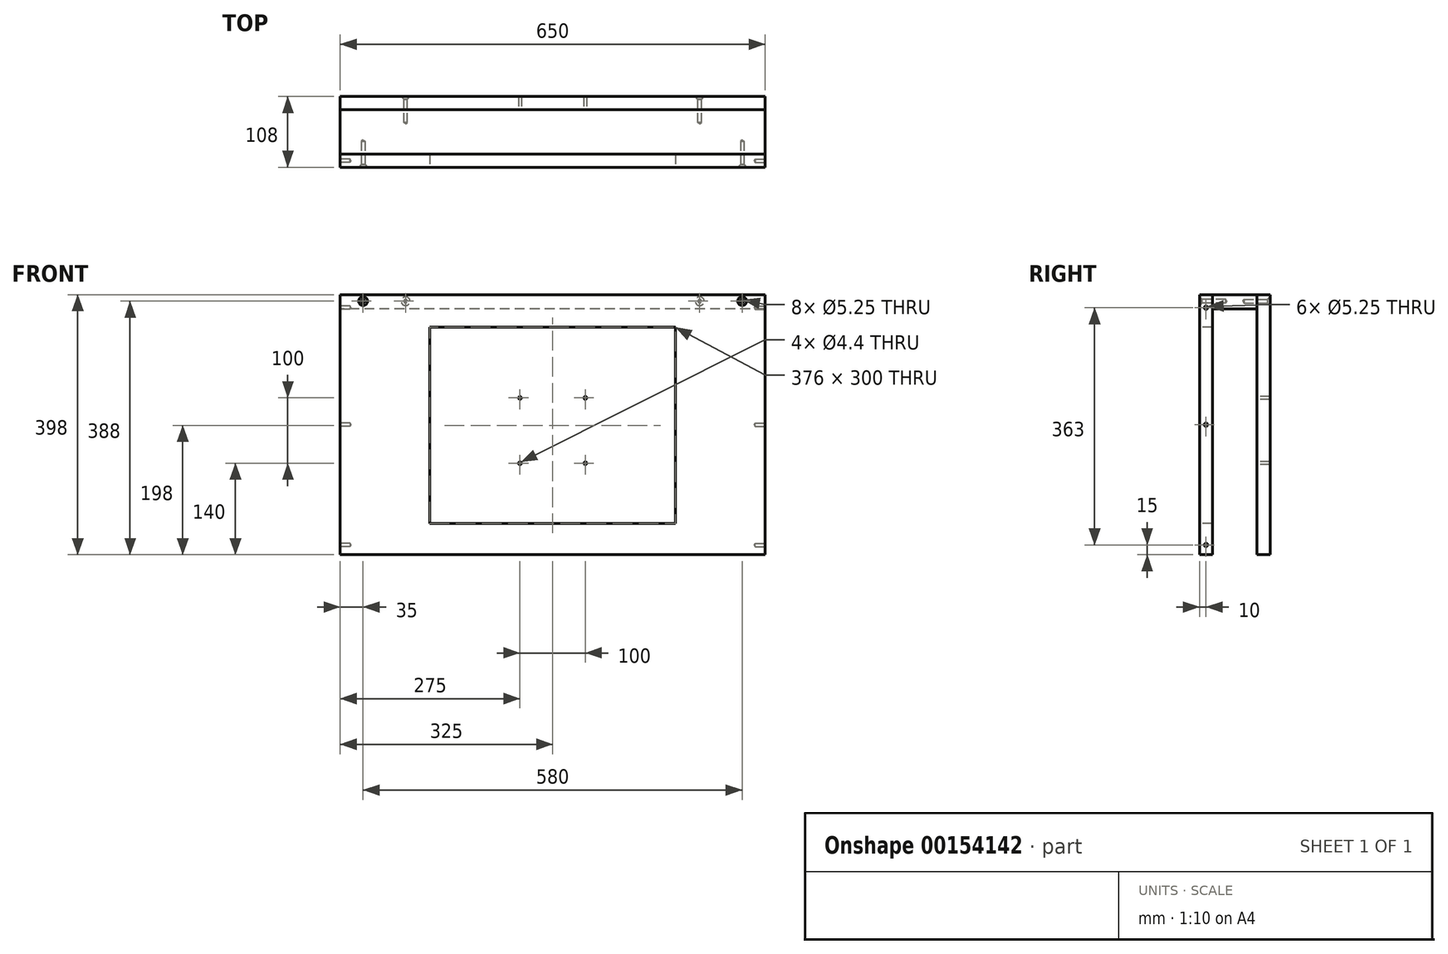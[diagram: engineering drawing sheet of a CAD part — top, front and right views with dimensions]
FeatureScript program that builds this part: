
annotation { "Feature Type Name" : "Feature", "Feature Type Description" : "" }
export const myFeature = defineFeature(function(context is Context, id is Id, definition is map)
    precondition{}
    {
        {
            var Q0;
            Q0=qCreatedBy(makeId("Front.planeOp"),FACE);
            var sketch = newSketch(context, id + "F0", { "sketchPlane" : qUnion([Q0])});
            skLineSegment(sketch, "E0.bottom", {"start": v(325, -199) * mm, "end": v(-325, -199) * mm});
            skLineSegment(sketch, "E0.top", {"start": v(325, 199) * mm, "end": v(-325, 199) * mm});
            skLineSegment(sketch, "E0.left", {"start": v(325, -199) * mm, "end": v(325, 199) * mm});
            skLineSegment(sketch, "E0.right", {"start": v(-325, -199) * mm, "end": v(-325, 199) * mm});
            skPoint(sketch, "E0.middle", {"position": v(0, 0) * mm});
            skLineSegment(sketch, "E1.bottom", {"start": v(-188, 149) * mm, "end": v(188, 149) * mm});
            skLineSegment(sketch, "E1.top", {"start": v(-188, -151) * mm, "end": v(188, -151) * mm});
            skLineSegment(sketch, "E1.left", {"start": v(-188, 149) * mm, "end": v(-188, -151) * mm});
            skLineSegment(sketch, "E1.right", {"start": v(188, 149) * mm, "end": v(188, -151) * mm});
            skPoint(sketch, "E2", {"position": v(-290, 189) * mm});
            skPoint(sketch, "E3", {"position": v(290, 189) * mm});
            skSolve(sketch);
        }
        {
            var Q0;
            Q0 = qSketchRegion(id + "F0", true);
            extrude(context, id + "F1", {"entities" : qUnion([Q0]), "oppositeDirection" : true, "depth" : 20 * mm});
        }
        {
            var Q0;
            Q0=makeQuery(id+"F1.opExtrude","SWEPT_FACE",FACE,{"disambiguationData":[OSD([sQuery(id+"F0.wireOp",EDGE,"E0.right")])]});
            var sketch = newSketch(context, id + "F2", { "sketchPlane" : qUnion([Q0])});
            skLineSegment(sketch, "E4.bottom", {"start": v(-20, 199) * mm, "end": v(0, 199) * mm});
            skLineSegment(sketch, "E4.top", {"start": v(-20, -199) * mm, "end": v(0, -199) * mm});
            skLineSegment(sketch, "E4.left", {"start": v(-20, 199) * mm, "end": v(-20, -199) * mm});
            skLineSegment(sketch, "E4.right", {"start": v(0, 199) * mm, "end": v(0, -199) * mm});
            skPoint(sketch, "E5", {"position": v(-10, 179) * mm});
            skPoint(sketch, "E6", {"position": v(-10, 0) * mm});
            skPoint(sketch, "E7", {"position": v(-10, -184) * mm});
            skSolve(sketch);
        }
        {
            var Q0;
            Q0=makeQuery(id+"F1.opExtrude","SWEPT_FACE",FACE,{"disambiguationData":[OSD([sQuery(id+"F0.wireOp",EDGE,"E0.left")])]});
            var sketch = newSketch(context, id + "F3", { "sketchPlane" : qUnion([Q0])});
            skPoint(sketch, "E8", {"position": v(10, 0) * mm});
            skPoint(sketch, "E9", {"position": v(10, 179) * mm});
            skPoint(sketch, "E10", {"position": v(10, -184) * mm});
            skSolve(sketch);
        }
        {
            var Q0;
            Q0=sQuery(id+"F2.wireOp",VERTEX,"E5");
            var Q1;
            Q1=sQuery(id+"F2.wireOp",VERTEX,"E6");
            var Q2;
            Q2=sQuery(id+"F2.wireOp",VERTEX,"E7");
            var Q3;
            Q3=sQuery(id+"F3.wireOp",VERTEX,"E9");
            var Q4;
            Q4=sQuery(id+"F3.wireOp",VERTEX,"E8");
            var Q5;
            Q5=sQuery(id+"F3.wireOp",VERTEX,"E10");
            var Q6;
            Q6=makeQuery(id+"F1.opExtrude","SWEPT_BODY",BODY,{"disambiguationData":[OSD([sQuery(id+"F0.wireOp",EDGE,"E0.bottom"),sQuery(id+"F0.wireOp",EDGE,"E0.top"),sQuery(id+"F0.wireOp",EDGE,"E0.left"),sQuery(id+"F0.wireOp",EDGE,"E0.right"),sQuery(id+"F0.wireOp",EDGE,"E1.bottom"),sQuery(id+"F0.wireOp",EDGE,"E1.top"),sQuery(id+"F0.wireOp",EDGE,"E1.left"),sQuery(id+"F0.wireOp",EDGE,"E1.right")])]});
            hole(context, id + "F4", {"style" : HoleStyle.SIMPLE, "endStyle" : HoleEndStyle.BLIND, "standardTappedOrClearance" : lookupTablePath({ "standard" : "ISO", "engagement" : "75%", "pitch" : "0.75 mm", "size" : "M6", "type" : "Tapped" }), "standardBlindInLast" : lookupTablePath({ "standard" : "ISO", "engagement" : "75%", "pitch" : "0.75 mm", "size" : "M6", "type" : "Tapped" }), "holeDiameter" : 5.25 * mm, "holeDepth" : 15 * mm, "locations" : qUnion([Q0, Q1, Q2, Q3, Q4, Q5]), "scope" : qUnion([Q6]), "majorDiameter" : 6 * mm});
        }
        {
            var Q0;
            Q0=makeQuery(id+"F1.opExtrude","CAP_FACE",FACE,{"disambiguationData":[OSD([sQuery(id+"F0.wireOp",EDGE,"E0.bottom"),sQuery(id+"F0.wireOp",EDGE,"E0.top"),sQuery(id+"F0.wireOp",EDGE,"E0.left"),sQuery(id+"F0.wireOp",EDGE,"E0.right"),sQuery(id+"F0.wireOp",EDGE,"E1.bottom"),sQuery(id+"F0.wireOp",EDGE,"E1.top"),sQuery(id+"F0.wireOp",EDGE,"E1.left"),sQuery(id+"F0.wireOp",EDGE,"E1.right")])],"isStart":false});
            var sketch = newSketch(context, id + "F5", { "sketchPlane" : qUnion([Q0])});
            skLineSegment(sketch, "E11.bottom", {"start": v(-325, 199) * mm, "end": v(325, 199) * mm});
            skLineSegment(sketch, "E11.top", {"start": v(-325, 177) * mm, "end": v(325, 177) * mm});
            skLineSegment(sketch, "E11.left", {"start": v(325, 199) * mm, "end": v(325, 177) * mm});
            skLineSegment(sketch, "E11.right", {"start": v(-325, 199) * mm, "end": v(-325, 177) * mm});
            skSolve(sketch);
        }
        {
            var Q0;
            Q0 = qSketchRegion(id + "F5", true);
            extrude(context, id + "F6", {"entities" : qUnion([Q0]), "depth" : 68 * mm});
        }
        {
            var Q0;
            Q0=makeQuery(id+"F6.opExtrude","CAP_FACE",FACE,{"disambiguationData":[OSD([sQuery(id+"F5.wireOp",EDGE,"E11.bottom"),sQuery(id+"F5.wireOp",EDGE,"E11.top"),sQuery(id+"F5.wireOp",EDGE,"E11.left"),sQuery(id+"F5.wireOp",EDGE,"E11.right")])],"isStart":false});
            var sketch = newSketch(context, id + "F7", { "sketchPlane" : qUnion([Q0])});
            skLineSegment(sketch, "E12.bottom", {"start": v(-325, 199) * mm, "end": v(325, 199) * mm});
            skLineSegment(sketch, "E12.top", {"start": v(-325, -199) * mm, "end": v(325, -199) * mm});
            skLineSegment(sketch, "E12.left", {"start": v(-325, 199) * mm, "end": v(-325, -199) * mm});
            skLineSegment(sketch, "E12.right", {"start": v(325, 199) * mm, "end": v(325, -199) * mm});
            skPoint(sketch, "E13", {"position": v(-50, 41) * mm});
            skPoint(sketch, "E14", {"position": v(-50, -59) * mm});
            skPoint(sketch, "E15", {"position": v(50, -59) * mm});
            skPoint(sketch, "E16", {"position": v(50, 41) * mm});
            skLineSegment(sketch, "E17", {"start": v(-50, -59) * mm, "end": v(50, -59) * mm});
            skLineSegment(sketch, "E18", {"start": v(-50, 41) * mm, "end": v(50, 41) * mm});
            skLineSegment(sketch, "E19", {"start": v(50, 41) * mm, "end": v(50, -59) * mm});
            skLineSegment(sketch, "E20", {"start": v(-50, -59) * mm, "end": v(-50, 41) * mm});
            skSolve(sketch);
        }
        {
            var Q0;
            Q0 = qSketchRegion(id + "F7", true);
            var Q1;
            Q1=makeQuery(id+"F7.imprint","IMPRINT",FACE,{"disambiguationData":[TD([[makeQuery(id+"F7.imprint","IMPRINT",EDGE,{"derivedFrom":sQuery(id+"F7.wireOp",EDGE,"E17")}),1.0]])]});
            extrude(context, id + "F8", {"entities" : qUnion([Q0, Q1]), "depth" : 20 * mm});
        }
        {
            var Q0;
            Q0=makeQuery(id+"F8.opExtrude","CAP_FACE",FACE,{"disambiguationData":[OSD([sQuery(id+"F7.wireOp",EDGE,"E12.bottom"),sQuery(id+"F7.wireOp",EDGE,"E12.top"),sQuery(id+"F7.wireOp",EDGE,"E12.left"),sQuery(id+"F7.wireOp",EDGE,"E12.right")])],"isStart":false});
            var sketch = newSketch(context, id + "F9", { "sketchPlane" : qUnion([Q0])});
            skLineSegment(sketch, "E21.bottom", {"start": v(-325, 199) * mm, "end": v(325, 199) * mm});
            skLineSegment(sketch, "E21.top", {"start": v(-325, -199) * mm, "end": v(325, -199) * mm});
            skLineSegment(sketch, "E21.left", {"start": v(-325, 199) * mm, "end": v(-325, -199) * mm});
            skLineSegment(sketch, "E21.right", {"start": v(325, 199) * mm, "end": v(325, -199) * mm});
            skPoint(sketch, "E22", {"position": v(-225, 189) * mm});
            skPoint(sketch, "E23", {"position": v(225, 189) * mm});
            skSolve(sketch);
        }
        {
            var Q0;
            Q0=sQuery(id+"F0.wireOp",VERTEX,"E2");
            var Q1;
            Q1=sQuery(id+"F0.wireOp",VERTEX,"E3");
            var Q2;
            Q2=sQuery(id+"F9.wireOp",VERTEX,"E22");
            var Q3;
            Q3=sQuery(id+"F9.wireOp",VERTEX,"E23");
            var Q4;
            Q4=makeQuery(id+"F1.opExtrude","SWEPT_BODY",BODY,{"disambiguationData":[OSD([sQuery(id+"F0.wireOp",EDGE,"E0.bottom"),sQuery(id+"F0.wireOp",EDGE,"E0.top"),sQuery(id+"F0.wireOp",EDGE,"E0.left"),sQuery(id+"F0.wireOp",EDGE,"E0.right"),sQuery(id+"F0.wireOp",EDGE,"E1.bottom"),sQuery(id+"F0.wireOp",EDGE,"E1.top"),sQuery(id+"F0.wireOp",EDGE,"E1.left"),sQuery(id+"F0.wireOp",EDGE,"E1.right")])]});
            var Q5;
            Q5=makeQuery(id+"F6.opExtrude","SWEPT_BODY",BODY,{"disambiguationData":[OSD([sQuery(id+"F5.wireOp",EDGE,"E11.bottom"),sQuery(id+"F5.wireOp",EDGE,"E11.top"),sQuery(id+"F5.wireOp",EDGE,"E11.left"),sQuery(id+"F5.wireOp",EDGE,"E11.right")])]});
            var Q6;
            Q6=makeQuery(id+"F8.opExtrude","SWEPT_BODY",BODY,{"disambiguationData":[OSD([sQuery(id+"F7.wireOp",EDGE,"E12.bottom"),sQuery(id+"F7.wireOp",EDGE,"E12.top"),sQuery(id+"F7.wireOp",EDGE,"E12.left"),sQuery(id+"F7.wireOp",EDGE,"E12.right")])]});
            hole(context, id + "F10", {"style" : HoleStyle.C_SINK, "endStyle" : HoleEndStyle.BLIND, "standardTappedOrClearance" : lookupTablePath({ "standard" : "ISO", "engagement" : "75%", "pitch" : "0.75 mm", "size" : "M6", "type" : "Tapped" }), "standardBlindInLast" : lookupTablePath({ "standard" : "ISO", "engagement" : "75%", "pitch" : "0.75 mm", "size" : "M6", "type" : "Tapped" }), "holeDiameter" : 5.25 * mm, "cSinkDiameter" : 13.44 * mm, "cSinkAngle" : 90 * degree, "holeDepth" : 40 * mm, "locations" : qUnion([Q0, Q1, Q2, Q3]), "scope" : qUnion([Q4, Q5, Q6]), "majorDiameter" : 6 * mm});
        }
        {
            var Q0;
            Q0=sQuery(id+"F7.wireOp",VERTEX,"E13");
            var Q1;
            Q1=sQuery(id+"F7.wireOp",VERTEX,"0c5c716c-c621-4fc1-a947-26692eb2ba86");
            var Q2;
            Q2=sQuery(id+"F7.wireOp",VERTEX,"0617914d-727d-4c80-badd-26484117caa5");
            var Q3;
            Q3=sQuery(id+"F7.wireOp",VERTEX,"96a15a45-20d3-4d19-b878-2d2536ee27f1");
            var Q4;
            Q4=sQuery(id+"F7.wireOp",VERTEX,"E16");
            var Q5;
            Q5=sQuery(id+"F7.wireOp",VERTEX,"E15");
            var Q6;
            Q6=sQuery(id+"F7.wireOp",VERTEX,"E14");
            var Q7;
            Q7=makeQuery(id+"F8.opExtrude","SWEPT_BODY",BODY,{"disambiguationData":[OSD([sQuery(id+"F7.wireOp",EDGE,"E12.bottom"),sQuery(id+"F7.wireOp",EDGE,"E12.top"),sQuery(id+"F7.wireOp",EDGE,"E12.left"),sQuery(id+"F7.wireOp",EDGE,"E12.right")])]});
            hole(context, id + "F11", {"style" : HoleStyle.SIMPLE, "endStyle" : HoleEndStyle.THROUGH, "oppositeDirection" : true, "standardTappedOrClearance" : lookupTablePath({ "standard" : "ISO", "fit" : "Normal", "size" : "M4", "type" : "Clearance" }), "standardBlindInLast" : lookupTablePath({ "fit" : "Standard", "standard" : "ISO", "size" : "M4", "type" : "Clearance" }), "holeDiameter" : 4.4 * mm, "locations" : qUnion([Q0, Q1, Q2, Q3, Q4, Q5, Q6]), "scope" : qUnion([Q7]), "isTappedThrough" : true});
        }
    });
